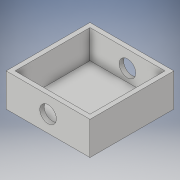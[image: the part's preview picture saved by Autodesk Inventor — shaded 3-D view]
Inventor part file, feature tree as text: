
AUTODESK INVENTOR PART (.ipt)
format: ipt  version: 2019.3 (Build 233278000, 278)  size: 241,664 bytes
history: native  units: mm
features: sketch x2, extrude x1, shell x1, hole x1
ambient origin geometry x8: Origin, YZ Plane, XZ Plane, XY Plane, X Axis, Y Axis, Z Axis, Center Point
bodies: Solid1 (feature_tree)
feature tree (5):
  extrude  "Extrusion1"  Depth=76.0mm
  shell  "Shell1"  Thickness=30.0mm
  hole  "Hole1"  [1 undecoded]
  sketch  "Sketch1"  dims[d0=76.0mm d1=76.0mm d2=30.0mm d3=0.0mm]
  sketch  "Sketch2"  dims[d4=4.0mm d5=15.0mm d6=15.0mm d7=6.0mm d8=4.0mm d9=2.0mm d10=90.0deg d11=8.0mm d12=20.594885mm]
note: 1 required parameter value undecoded (feature->parameter linkage not recoverable at this tier; creation-order binding heuristic only, values carry confidence <= 0.55)
